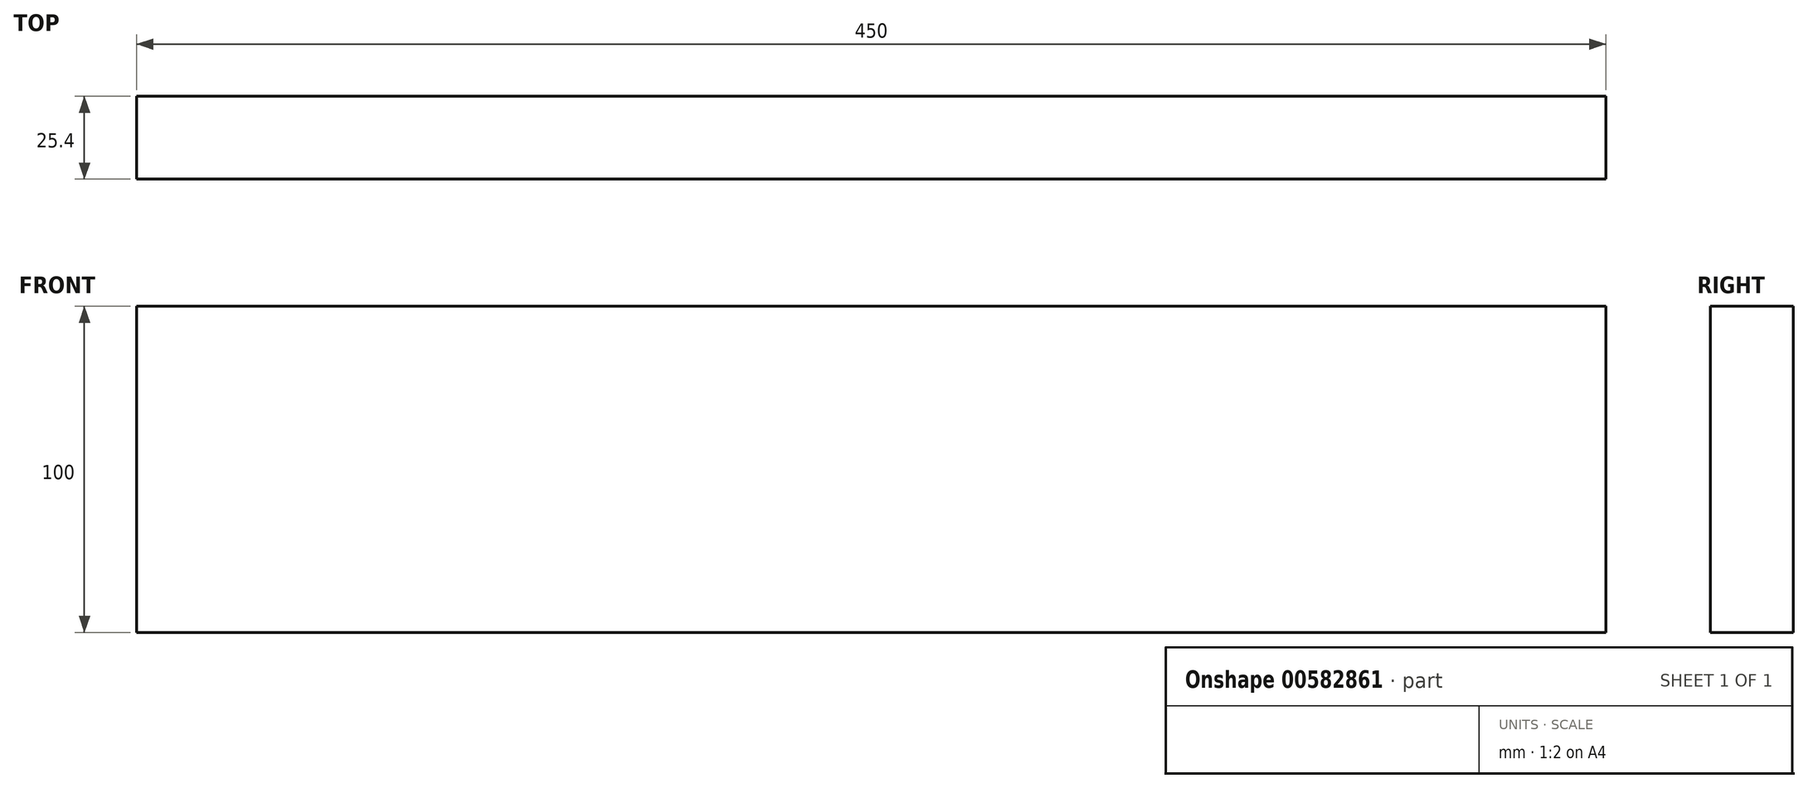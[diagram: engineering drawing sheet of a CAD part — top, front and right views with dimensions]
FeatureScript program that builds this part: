
annotation { "Feature Type Name" : "Feature", "Feature Type Description" : "" }
export const myFeature = defineFeature(function(context is Context, id is Id, definition is map)
    precondition{}
    {
        {
            var Q0;
            Q0=qCreatedBy(makeId("Front.planeOp"),FACE);
            var sketch = newSketch(context, id + "F0", { "sketchPlane" : qUnion([Q0])});
            skLineSegment(sketch, "E0.bottom", {"start": v(-169.77, 82.94) * mm, "end": v(280.23, 82.94) * mm});
            skLineSegment(sketch, "E0.top", {"start": v(-169.77, -17.06) * mm, "end": v(280.23, -17.06) * mm});
            skLineSegment(sketch, "E0.left", {"start": v(-169.77, 82.94) * mm, "end": v(-169.77, -17.06) * mm});
            skLineSegment(sketch, "E0.right", {"start": v(280.23, 82.94) * mm, "end": v(280.23, -17.06) * mm});
            skSolve(sketch);
        }
        {
            var Q0;
            Q0=makeQuery(id+"F0.imprint","IMPRINT",FACE,{"disambiguationData":[TD([[makeQuery(id+"F0.imprint","IMPRINT",EDGE,{"derivedFrom":sQuery(id+"F0.wireOp",EDGE,"E0.bottom")}),-1.0]])]});
            extrude(context, id + "F1", {"entities" : qUnion([Q0]), "depth" : 25.4 * mm, "offsetDistance" : 25.4 * mm});
        }
    });
